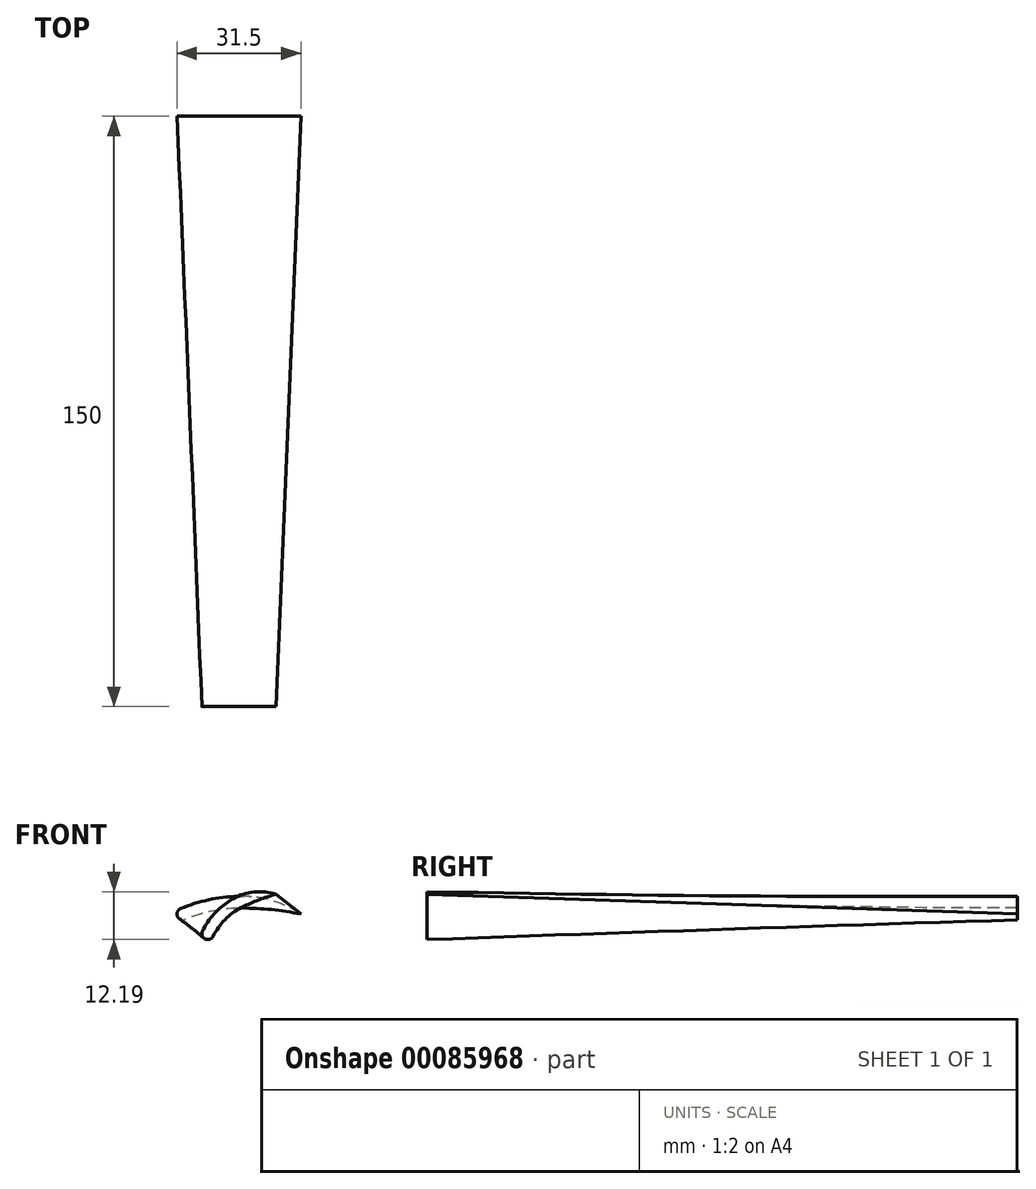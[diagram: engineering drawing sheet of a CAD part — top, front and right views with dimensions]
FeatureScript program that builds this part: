
annotation { "Feature Type Name" : "Feature", "Feature Type Description" : "" }
export const myFeature = defineFeature(function(context is Context, id is Id, definition is map)
    precondition{}
    {
        {
            var Q0;
            Q0=qCreatedBy(makeId("Front.planeOp"),FACE);
            var sketch = newSketch(context, id + "F0", { "sketchPlane" : qUnion([Q0])});
            skLineSegment(sketch, "E0", {"start": v(0, 0) * mm, "end": v(15, 0) * mm, "construction": true});
            skLineSegment(sketch, "E1", {"start": v(0, 0) * mm, "end": v(-15, 0) * mm, "construction": true});
            skLineSegment(sketch, "E2", {"start": v(-15, 3) * mm, "end": v(15, 3) * mm, "construction": true});
            skArc(sketch, "E3", {"start": v(15, 0) * mm, "mid": v(0, 3) * mm, "end": v(-15, 0) * mm});
            skArc(sketch, "E4.0", {"start": v(15.58, 1.38) * mm, "mid": v(7.94, 3.71) * mm, "end": v(0, 4.5) * mm});
            skArc(sketch, "E5.0", {"start": v(14.4, -1.38) * mm, "mid": v(7.35, 0.77) * mm, "end": v(0, 1.5) * mm});
            skArc(sketch, "E6", {"start": v(-15.58, 1.38) * mm, "mid": v(-16.38, -0.58) * mm, "end": v(-14.42, -1.38) * mm});
            skLineSegment(sketch, "E7", {"start": v(0, 0) * mm, "end": v(0, 1.5) * mm, "construction": true});
            skPoint(sketch, "E7.endSnap0", {"position": v(0, 3) * mm});
            skArc(sketch, "E8", {"start": v(0, 4.5) * mm, "mid": v(-7.94, 3.71) * mm, "end": v(-15.58, 1.38) * mm});
            skLineSegment(sketch, "E9", {"start": v(0, 1.5) * mm, "end": v(0, 10.55) * mm, "construction": true});
            skArc(sketch, "E10", {"start": v(0, 4.5) * mm, "mid": v(7.83, 3.35) * mm, "end": v(15, 0) * mm});
            skArc(sketch, "E11", {"start": v(0, 1.5) * mm, "mid": v(-7.35, 0.77) * mm, "end": v(-14.42, -1.38) * mm});
            skArc(sketch, "E12", {"start": v(0, 1.5) * mm, "mid": v(7.54, 1.12) * mm, "end": v(15, 0) * mm});
            skSolve(sketch);
        }
        {
            var Q0;
            Q0=qCreatedBy(makeId("Front.planeOp"),FACE);
            cPlane(context, id + "F1", {"entities" : qUnion([Q0]), "cplaneType" : CPlaneType.OFFSET, "offset" : 150 * mm, "width" : 150 * mm, "height" : 150 * mm});
        }
        {
            var Q0;
            Q0=qCreatedBy(id+"F1.planeOp",FACE);
            var sketch = newSketch(context, id + "F2", { "sketchPlane" : qUnion([Q0])});
            skLineSegment(sketch, "E13", {"start": v(0, 0) * mm, "end": v(-33.45, 0) * mm, "construction": true});
            skCircle(sketch, "E14", {"center": v(0, 0) * mm, "radius": 10 * mm, "construction": true});
            skLineSegment(sketch, "E15", {"start": v(8.66, 5) * mm, "end": v(-8.66, -5) * mm, "construction": true});
            skLineSegment(sketch, "E16", {"start": v(0, 0) * mm, "end": v(-1.5, 2.6) * mm, "construction": true});
            skArc(sketch, "E17", {"start": v(8.66, 5) * mm, "mid": v(-1.5, 2.6) * mm, "end": v(-8.66, -5) * mm, "construction": true});
            skArc(sketch, "E18.0", {"start": v(8.75, 6.5) * mm, "mid": v(3.06, 6) * mm, "end": v(-2.25, 3.9) * mm});
            skArc(sketch, "E19.0", {"start": v(8.57, 3.5) * mm, "mid": v(4.24, 3.2) * mm, "end": v(0.13, 1.77) * mm});
            skArc(sketch, "E20", {"start": v(-10, -4.33) * mm, "mid": v(-9.33, -6.34) * mm, "end": v(-7.32, -5.67) * mm});
            skLineSegment(sketch, "E21", {"start": v(-8.66, -5) * mm, "end": v(-10, -4.33) * mm, "construction": true});
            skLineSegment(sketch, "E22", {"start": v(-8.66, -5) * mm, "end": v(-7.32, -5.67) * mm, "construction": true});
            skLineSegment(sketch, "E23", {"start": v(8.66, 5) * mm, "end": v(8.75, 6.5) * mm, "construction": true});
            skLineSegment(sketch, "E24", {"start": v(8.66, 5) * mm, "end": v(8.57, 3.5) * mm, "construction": true});
            skLineSegment(sketch, "E25", {"start": v(-1.5, 2.6) * mm, "end": v(-2.25, 3.9) * mm, "construction": true});
            skLineSegment(sketch, "E26", {"start": v(-1.5, 2.6) * mm, "end": v(-0.75, 1.3) * mm, "construction": true});
            skArc(sketch, "E27", {"start": v(-2.25, 3.9) * mm, "mid": v(-6.73, 0.35) * mm, "end": v(-10, -4.33) * mm});
            skArc(sketch, "E28", {"start": v(-2.25, 3.9) * mm, "mid": v(3.09, 5.62) * mm, "end": v(8.66, 5) * mm});
            skLineSegment(sketch, "E29.0", {"start": v(0.87, 0.5) * mm, "end": v(-0.63, 3.1) * mm, "construction": true});
            skArc(sketch, "E30", {"start": v(0.13, 1.77) * mm, "mid": v(-4.2, -1.35) * mm, "end": v(-7.32, -5.67) * mm});
            skArc(sketch, "E31", {"start": v(0.13, 1.77) * mm, "mid": v(4.31, 3.6) * mm, "end": v(8.66, 5) * mm});
            skSolve(sketch);
        }
        {
            var Q0;
            Q0=makeQuery(id+"F0.imprint","IMPRINT",FACE,{"disambiguationData":[TD([[makeQuery(id+"F0.imprint","IMPRINT",EDGE,{"derivedFrom":sQuery(id+"F0.wireOp",EDGE,"E6")}),1.0]])]});
            var Q1;
            Q1=makeQuery(id+"F2.imprint","IMPRINT",FACE,{"disambiguationData":[TD([[makeQuery(id+"F2.imprint","IMPRINT",EDGE,{"derivedFrom":sQuery(id+"F2.wireOp",EDGE,"E20")}),1.0]])]});
            loft(context, id + "F3", {"sheetProfilesArray" : [{ "sheetProfileEntities" : qUnion([Q0]) }, { "sheetProfileEntities" : qUnion([Q1]) }]});
        }
    });
